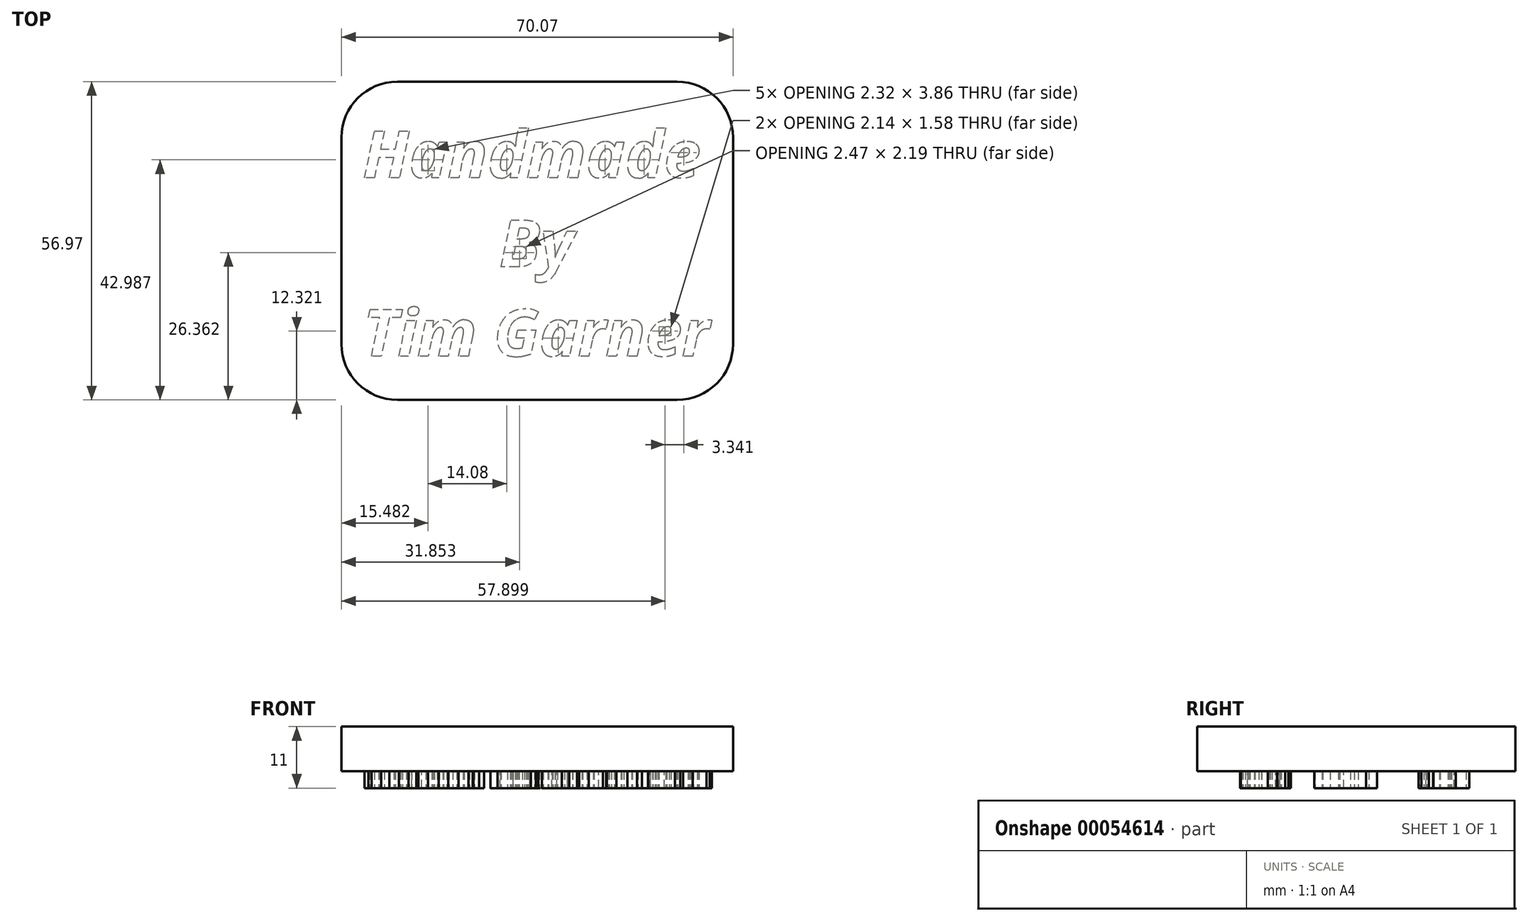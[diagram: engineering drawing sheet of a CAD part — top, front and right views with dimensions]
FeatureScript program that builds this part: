
annotation { "Feature Type Name" : "Feature", "Feature Type Description" : "" }
export const myFeature = defineFeature(function(context is Context, id is Id, definition is map)
    precondition{}
    {
        {
            var Q0;
            Q0=qCreatedBy(makeId("Top.planeOp"),FACE);
            var sketch = newSketch(context, id + "F0", { "sketchPlane" : qUnion([Q0])});
            skText(sketch, "E0", { "text": "Handmade\n        By\nTim Garner", "fontName": "OpenSans-BoldItalic.ttf"});
            const initialGuessF0  = {"E0": [0, 6e-05, 1, 0, 0.00846]};
            skSetInitialGuess(sketch, initialGuessF0);
            skSolve(sketch);
        }
        {
            var Q0;
            Q0 = qSketchRegion(id + "F0", true);
            extrude(context, id + "F1", {"entities" : qUnion([Q0]), "depth" : 3 * mm});
        }
        {
            var Q0;
            Q0=makeQuery(id+"F1.opExtrude","CAP_FACE",FACE,{"disambiguationData":[OSD([sQuery(id+"F0.wireOp",EDGE,"E0.sketch_text.stroke-226"),sQuery(id+"F0.wireOp",EDGE,"E0.sketch_text.stroke-227"),sQuery(id+"F0.wireOp",EDGE,"E0.sketch_text.stroke-228"),sQuery(id+"F0.wireOp",EDGE,"E0.sketch_text.stroke-229"),sQuery(id+"F0.wireOp",EDGE,"E0.sketch_text.stroke-230"),sQuery(id+"F0.wireOp",EDGE,"E0.sketch_text.stroke-231"),sQuery(id+"F0.wireOp",EDGE,"E0.sketch_text.stroke-232"),sQuery(id+"F0.wireOp",EDGE,"E0.sketch_text.stroke-233")])],"isStart":false});
            var sketch = newSketch(context, id + "F2", { "sketchPlane" : qUnion([Q0])});
            skLineSegment(sketch, "E1.bottom", {"start": v(66.24, 17.25) * mm, "end": v(-3.83, 17.25) * mm});
            skLineSegment(sketch, "E1.top", {"start": v(66.24, -39.72) * mm, "end": v(-3.83, -39.72) * mm});
            skLineSegment(sketch, "E1.left", {"start": v(66.24, 17.25) * mm, "end": v(66.24, -39.72) * mm});
            skLineSegment(sketch, "E1.right", {"start": v(-3.83, 17.25) * mm, "end": v(-3.83, -39.72) * mm});
            skSolve(sketch);
        }
        {
            var Q0;
            Q0=makeQuery(id+"F2.imprint","IMPRINT",FACE,{"disambiguationData":[TD([[makeQuery(id+"F2.imprint","IMPRINT",EDGE,{"derivedFrom":sQuery(id+"F2.wireOp",EDGE,"E1.bottom")}),1.0]])]});
            var Q1;
            Q1=makeQuery(id+"F2.imprint","IMPRINT",FACE,{"disambiguationData":[TD([[makeQuery(id+"F2.imprint","IMPRINT",EDGE,{"derivedFrom":makeQuery(id+"F1.opExtrude","CAP_EDGE",EDGE,{"disambiguationData":[OSD([sQuery(id+"F0.wireOp",EDGE,"E0.sketch_text.stroke-226")])],"isStart":false})}),-1.0]])]});
            extrude(context, id + "F3", {"entities" : qUnion([Q0, Q1]), "depth" : 8 * mm});
        }
        {
            var Q0;
            Q0=makeQuery(id+"F3.opExtrude","SWEPT_EDGE",EDGE,{"disambiguationData":[OSD([sQuery(id+"F2.wireOp",EDGE,"E1.top"),sQuery(id+"F2.wireOp",EDGE,"E1.right")])]});
            var Q1;
            Q1=makeQuery(id+"F3.opExtrude","SWEPT_EDGE",EDGE,{"disambiguationData":[OSD([sQuery(id+"F2.wireOp",EDGE,"E1.bottom"),sQuery(id+"F2.wireOp",EDGE,"E1.right")])]});
            var Q2;
            Q2=makeQuery(id+"F3.opExtrude","SWEPT_EDGE",EDGE,{"disambiguationData":[OSD([sQuery(id+"F2.wireOp",EDGE,"E1.bottom"),sQuery(id+"F2.wireOp",EDGE,"E1.left")])]});
            var Q3;
            Q3=makeQuery(id+"F3.opExtrude","SWEPT_EDGE",EDGE,{"disambiguationData":[OSD([sQuery(id+"F2.wireOp",EDGE,"E1.top"),sQuery(id+"F2.wireOp",EDGE,"E1.left")])]});
            fillet(context, id + "F4", {"entities" : qUnion([Q0, Q1, Q2, Q3]), "radius" : 10 * mm, "tangentPropagation" : true, "allowEdgeOverflow" : false});
        }
    });
